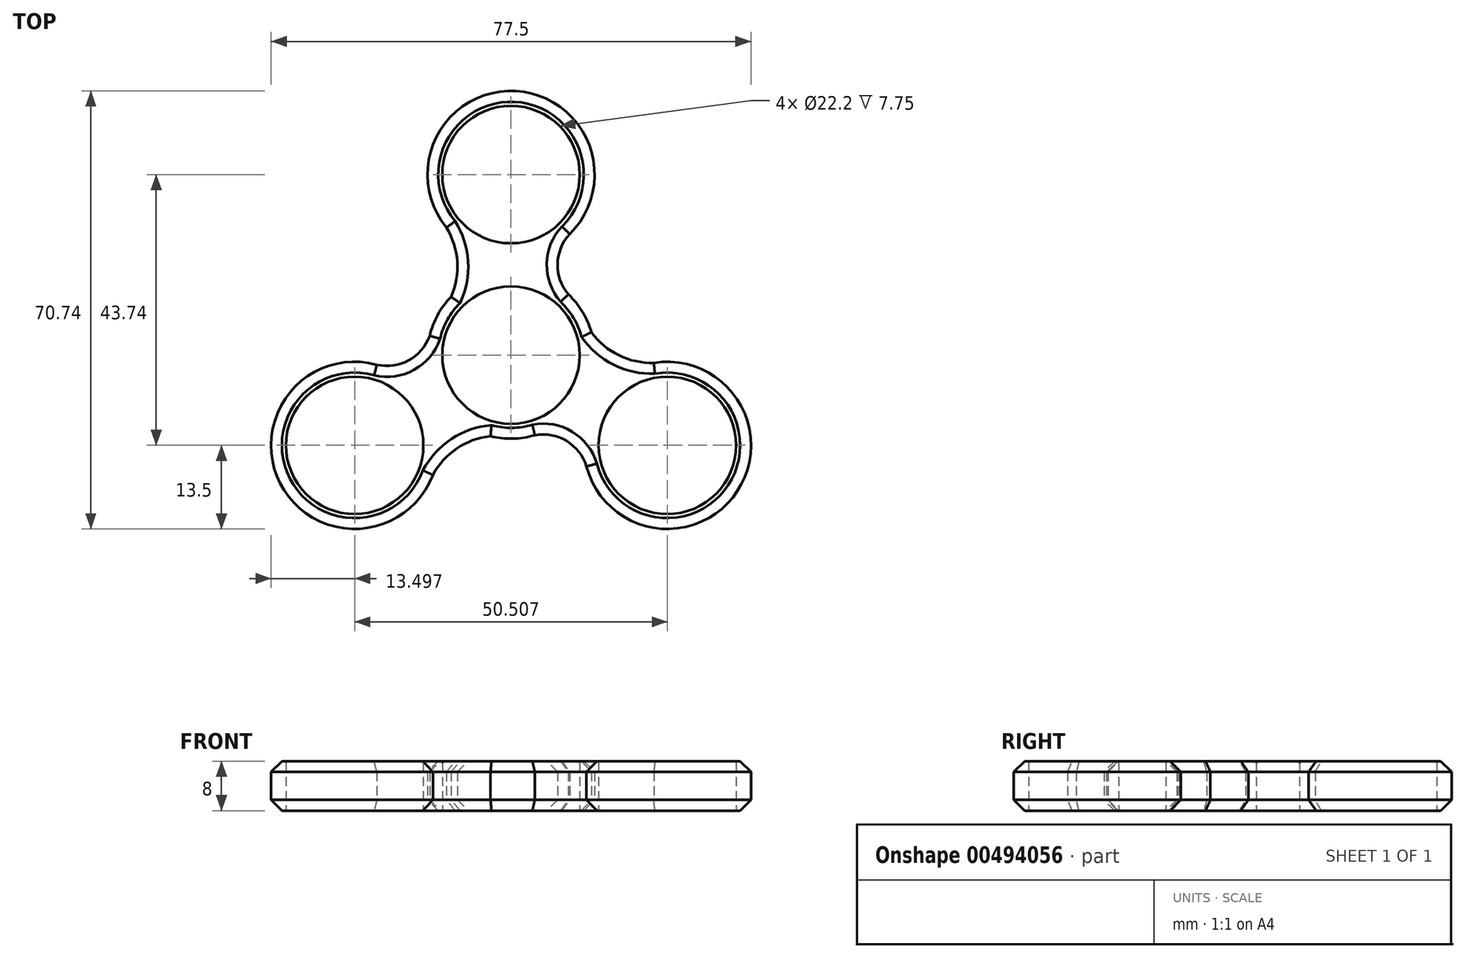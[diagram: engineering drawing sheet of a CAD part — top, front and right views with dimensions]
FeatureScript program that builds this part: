
annotation { "Feature Type Name" : "Feature", "Feature Type Description" : "" }
export const myFeature = defineFeature(function(context is Context, id is Id, definition is map)
    precondition{}
    {
        {
            var Q0;
            Q0=qCreatedBy(makeId("Top.planeOp"),FACE);
            var sketch = newSketch(context, id + "F0", { "sketchPlane" : qUnion([Q0])});
            skCircle(sketch, "E0", {"center": v(0, 0) * mm, "radius": 11.1 * mm});
            skCircle(sketch, "E1", {"center": v(0, 0) * mm, "radius": 13.5 * mm});
            skCircle(sketch, "E2", {"center": v(0, 29.16) * mm, "radius": 11.1 * mm});
            skCircle(sketch, "E3", {"center": v(0, 29.16) * mm, "radius": 13.5 * mm});
            skArc(sketch, "E4", {"start": v(-9.69, 9.4) * mm, "mid": v(-8.68, 15.1) * mm, "end": v(-10.44, 20.6) * mm});
            skArc(sketch, "E5", {"start": v(9.76, 19.84) * mm, "mid": v(7.53, 14.92) * mm, "end": v(9.27, 9.81) * mm});
            skCircle(sketch, "E6.1.0", {"center": v(-25.25, -14.58) * mm, "radius": 13.5 * mm});
            skCircle(sketch, "E6.1.1", {"center": v(-25.25, -14.58) * mm, "radius": 11.1 * mm});
            skArc(sketch, "E6.1.2", {"start": v(-3.3, -13.1) * mm, "mid": v(-8.73, -15.07) * mm, "end": v(-12.62, -19.35) * mm});
            skArc(sketch, "E6.1.3", {"start": v(-22.06, -1.46) * mm, "mid": v(-16.69, -0.94) * mm, "end": v(-13.13, 3.13) * mm});
            skCircle(sketch, "E6.2.0", {"center": v(25.25, -14.58) * mm, "radius": 13.5 * mm});
            skCircle(sketch, "E6.2.1", {"center": v(25.25, -14.58) * mm, "radius": 11.1 * mm});
            skArc(sketch, "E6.2.2", {"start": v(12.99, 3.7) * mm, "mid": v(17.41, -0.03) * mm, "end": v(23.07, -1.26) * mm});
            skArc(sketch, "E6.2.3", {"start": v(12.3, -18.37) * mm, "mid": v(9.16, -13.98) * mm, "end": v(3.86, -12.94) * mm});
            skSolve(sketch);
        }
        {
            var Q0;
            Q0=qSketchRegion(id+"F0",true);
            extrude(context, id + "F1", {"entities" : qUnion([Q0]), "depth" : 8 * mm});
        }
        {
            var Q0;
            Q0=makeQuery(id+"F1.opExtrude","CAP_EDGE",EDGE,{"disambiguationData":[OSD([sQuery(id+"F0.wireOp",EDGE,"E6.1.0")])],"isStart":true});
            var Q1;
            Q1=makeQuery(id+"F1.opExtrude","CAP_EDGE",EDGE,{"disambiguationData":[OSD([sQuery(id+"F0.wireOp",EDGE,"E6.1.3")])],"isStart":true});
            var Q2;
            Q2=makeQuery(id+"F1.opExtrude","CAP_EDGE",EDGE,{"disambiguationData":[OSD([sQuery(id+"F0.wireOp",EDGE,"E6.1.2")])],"isStart":true});
            var Q3;
            {var subQ0=sQuery(id+"F0.wireOp",EDGE,"E1");Q3=makeQuery(id+"F1.opExtrude","CAP_EDGE",EDGE,{"disambiguationData":[OSD([subQ0]),TDD([makeQuery(id+"F0.imprint","IMPRINT",EDGE,{"disambiguationData":[TD([[makeQuery(id+"F0.imprint","INTERSECT",VERTEX,{"derivedFrom":[subQ0,sQuery(id+"F0.wireOp",EDGE,"E6.1.2")]}),-1.0]])],"derivedFrom":subQ0})])],"isStart":true});}
            var Q4;
            Q4=makeQuery(id+"F1.opExtrude","CAP_EDGE",EDGE,{"disambiguationData":[OSD([sQuery(id+"F0.wireOp",EDGE,"E6.2.3")])],"isStart":true});
            var Q5;
            Q5=makeQuery(id+"F1.opExtrude","CAP_EDGE",EDGE,{"disambiguationData":[OSD([sQuery(id+"F0.wireOp",EDGE,"E6.2.0")])],"isStart":true});
            var Q6;
            Q6=makeQuery(id+"F1.opExtrude","CAP_EDGE",EDGE,{"disambiguationData":[OSD([sQuery(id+"F0.wireOp",EDGE,"E6.2.2")])],"isStart":true});
            var Q7;
            {var subQ0=sQuery(id+"F0.wireOp",EDGE,"E1");Q7=makeQuery(id+"F1.opExtrude","CAP_EDGE",EDGE,{"disambiguationData":[OSD([subQ0]),TDD([makeQuery(id+"F0.imprint","IMPRINT",EDGE,{"disambiguationData":[TD([[makeQuery(id+"F0.imprint","INTERSECT",VERTEX,{"derivedFrom":[subQ0,sQuery(id+"F0.wireOp",EDGE,"E5")]}),1.0]])],"derivedFrom":subQ0})])],"isStart":true});}
            var Q8;
            Q8=makeQuery(id+"F1.opExtrude","CAP_EDGE",EDGE,{"disambiguationData":[OSD([sQuery(id+"F0.wireOp",EDGE,"E5")])],"isStart":true});
            var Q9;
            Q9=makeQuery(id+"F1.opExtrude","CAP_EDGE",EDGE,{"disambiguationData":[OSD([sQuery(id+"F0.wireOp",EDGE,"E3")])],"isStart":true});
            var Q10;
            Q10=makeQuery(id+"F1.opExtrude","CAP_EDGE",EDGE,{"disambiguationData":[OSD([sQuery(id+"F0.wireOp",EDGE,"E4")])],"isStart":true});
            var Q11;
            {var subQ0=sQuery(id+"F0.wireOp",EDGE,"E1");Q11=makeQuery(id+"F1.opExtrude","CAP_EDGE",EDGE,{"disambiguationData":[OSD([subQ0]),TDD([makeQuery(id+"F0.imprint","IMPRINT",EDGE,{"disambiguationData":[TD([[makeQuery(id+"F0.imprint","INTERSECT",VERTEX,{"derivedFrom":[subQ0,sQuery(id+"F0.wireOp",EDGE,"E4")]}),-1.0]])],"derivedFrom":subQ0})])],"isStart":true});}
            var Q12;
            Q12=makeQuery(id+"F1.opExtrude","CAP_EDGE",EDGE,{"disambiguationData":[OSD([sQuery(id+"F0.wireOp",EDGE,"E3")])],"isStart":false});
            var Q13;
            Q13=makeQuery(id+"F1.opExtrude","CAP_EDGE",EDGE,{"disambiguationData":[OSD([sQuery(id+"F0.wireOp",EDGE,"E5")])],"isStart":false});
            var Q14;
            {var subQ0=sQuery(id+"F0.wireOp",EDGE,"E1");Q14=makeQuery(id+"F1.opExtrude","CAP_EDGE",EDGE,{"disambiguationData":[OSD([subQ0]),TDD([makeQuery(id+"F0.imprint","IMPRINT",EDGE,{"disambiguationData":[TD([[makeQuery(id+"F0.imprint","INTERSECT",VERTEX,{"derivedFrom":[subQ0,sQuery(id+"F0.wireOp",EDGE,"E5")]}),1.0]])],"derivedFrom":subQ0})])],"isStart":false});}
            var Q15;
            Q15=makeQuery(id+"F1.opExtrude","CAP_EDGE",EDGE,{"disambiguationData":[OSD([sQuery(id+"F0.wireOp",EDGE,"E6.2.2")])],"isStart":false});
            var Q16;
            Q16=makeQuery(id+"F1.opExtrude","CAP_EDGE",EDGE,{"disambiguationData":[OSD([sQuery(id+"F0.wireOp",EDGE,"E6.2.0")])],"isStart":false});
            var Q17;
            Q17=makeQuery(id+"F1.opExtrude","CAP_EDGE",EDGE,{"disambiguationData":[OSD([sQuery(id+"F0.wireOp",EDGE,"E4")])],"isStart":false});
            var Q18;
            {var subQ0=sQuery(id+"F0.wireOp",EDGE,"E1");Q18=makeQuery(id+"F1.opExtrude","CAP_EDGE",EDGE,{"disambiguationData":[OSD([subQ0]),TDD([makeQuery(id+"F0.imprint","IMPRINT",EDGE,{"disambiguationData":[TD([[makeQuery(id+"F0.imprint","INTERSECT",VERTEX,{"derivedFrom":[subQ0,sQuery(id+"F0.wireOp",EDGE,"E4")]}),-1.0]])],"derivedFrom":subQ0})])],"isStart":false});}
            var Q19;
            Q19=makeQuery(id+"F1.opExtrude","CAP_EDGE",EDGE,{"disambiguationData":[OSD([sQuery(id+"F0.wireOp",EDGE,"E6.1.3")])],"isStart":false});
            var Q20;
            Q20=makeQuery(id+"F1.opExtrude","CAP_EDGE",EDGE,{"disambiguationData":[OSD([sQuery(id+"F0.wireOp",EDGE,"E6.1.0")])],"isStart":false});
            var Q21;
            Q21=makeQuery(id+"F1.opExtrude","CAP_EDGE",EDGE,{"disambiguationData":[OSD([sQuery(id+"F0.wireOp",EDGE,"E6.1.2")])],"isStart":false});
            var Q22;
            Q22=makeQuery(id+"F1.opExtrude","CAP_EDGE",EDGE,{"disambiguationData":[OSD([sQuery(id+"F0.wireOp",EDGE,"E6.2.3")])],"isStart":false});
            var Q23;
            {var subQ0=sQuery(id+"F0.wireOp",EDGE,"E1");Q23=makeQuery(id+"F1.opExtrude","CAP_EDGE",EDGE,{"disambiguationData":[OSD([subQ0]),TDD([makeQuery(id+"F0.imprint","IMPRINT",EDGE,{"disambiguationData":[TD([[makeQuery(id+"F0.imprint","INTERSECT",VERTEX,{"derivedFrom":[subQ0,sQuery(id+"F0.wireOp",EDGE,"E6.1.2")]}),-1.0]])],"derivedFrom":subQ0})])],"isStart":false});}
            chamfer(context, id + "F2", {"entities" : qUnion([Q0, Q1, Q2, Q3, Q4, Q5, Q6, Q7, Q8, Q9, Q10, Q11, Q12, Q13, Q14, Q15, Q16, Q17, Q18, Q19, Q20, Q21, Q22, Q23]), "chamferType" : ChamferType.OFFSET_ANGLE, "width" : 1.75 * mm, "oppositeDirection" : false, "angle" : 45 * degree, "tangentPropagation" : true});
        }
        {
            var Q0;
            Q0=makeQuery(id+"F1.opExtrude","CAP_EDGE",EDGE,{"disambiguationData":[OSD([sQuery(id+"F0.wireOp",EDGE,"E2")])],"isStart":false});
            var Q1;
            Q1=makeQuery(id+"F1.opExtrude","CAP_EDGE",EDGE,{"disambiguationData":[OSD([sQuery(id+"F0.wireOp",EDGE,"E6.1.1")])],"isStart":false});
            var Q2;
            Q2=makeQuery(id+"F1.opExtrude","CAP_EDGE",EDGE,{"disambiguationData":[OSD([sQuery(id+"F0.wireOp",EDGE,"E6.2.1")])],"isStart":false});
            var Q3;
            Q3=makeQuery(id+"F1.opExtrude","CAP_EDGE",EDGE,{"disambiguationData":[OSD([sQuery(id+"F0.wireOp",EDGE,"E0")])],"isStart":false});
            fillet(context, id + "F3", {"entities" : qUnion([Q0, Q1, Q2, Q3]), "radius" : 0.25 * mm, "tangentPropagation" : true, "allowEdgeOverflow" : false});
        }
    });
